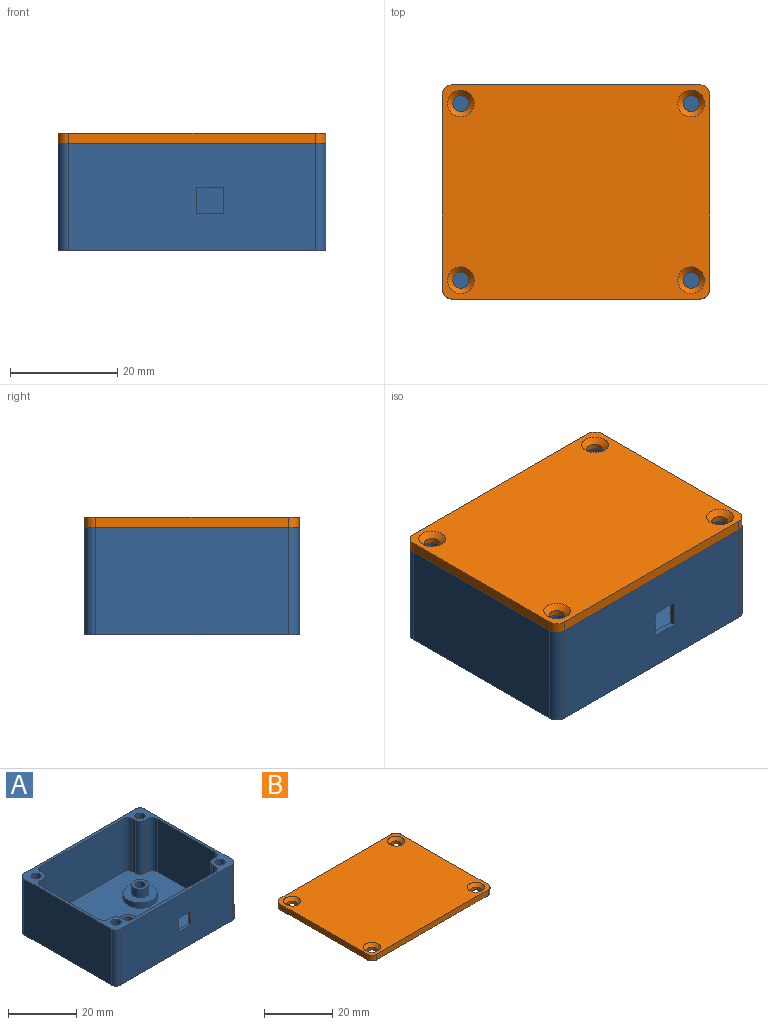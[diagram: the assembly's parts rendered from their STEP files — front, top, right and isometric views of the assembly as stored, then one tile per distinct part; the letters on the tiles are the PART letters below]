
ASSEMBLY  parts=2 mates=1
PART A: 71 faces, bbox 50x40x20 mm
  f0: plane 34x19mm, normal (0,1,0), area 621mm2, adj f4,f8,f56,f58,f67,f68,f69,f70
  f1: plane 46x20mm, normal (0,-1,0), area 895mm2, adj f8,f12,f52,f53,f67,f68,f69,f70
  f2: cylinder r=1.5mm len=4mm, axis (0,0,-1), area 37.7mm2, adj f30,f50
  f3: cylinder r=1.5mm len=4mm, axis (0,0,-1), area 37.7mm2, adj f32,f43
  f4: plane 48x38mm, normal (0,0,1), area 1563.5mm2, adj f0,f5,f6,f7,f13,f14,f15,f16
  f5: plane 24x19mm, normal (-1,0,0), area 456mm2, adj f4,f8,f60,f61
  f6: plane 34x19mm, normal (0,-1,0), area 646mm2, adj f4,f8,f62,f64
  f7: plane 24x19mm, normal (1,0,0), area 456mm2, adj f4,f8,f57,f66
  f8: plane 50x40mm, normal (0,0,1), area 247.7mm2, adj f0,f1,f5,f6,f7,f9,f10,f11
  f9: plane 46x20mm, normal (0,1,0), area 920mm2, adj f8,f12,f51,f54
  f10: plane 36x20mm, normal (-1,0,0), area 720mm2, adj f8,f12,f51,f52
  f11: plane 36x20mm, normal (1,0,0), area 720mm2, adj f8,f12,f53,f54
  f12: plane 50x40mm, normal (0,0,-1), area 1949.8mm2, adj f1,f9,f10,f11,f37,f38,f39,f40
  f13: plane 19x1mm, normal (0,-1,0), area 19mm2, adj f4,f8,f65,f66
  f14: plane 19x1mm, normal (1,0,0), area 19mm2, adj f4,f8,f64,f65
  f15: plane 19x1mm, normal (0,-1,0), area 19mm2, adj f4,f8,f61,f63
  f16: plane 19x1mm, normal (-1,0,0), area 19mm2, adj f4,f8,f62,f63
  f17: plane 19x1mm, normal (0,1,0), area 19mm2, adj f4,f8,f59,f60
  f18: plane 19x1mm, normal (-1,0,0), area 19mm2, adj f4,f8,f58,f59
  f19: plane 19x1mm, normal (0,1,0), area 19mm2, adj f4,f8,f55,f57
  f20: plane 19x1mm, normal (1,0,0), area 19mm2, adj f4,f8,f55,f56
  f21: cylinder r=1.5mm len=10mm, axis (0,0,1), area 94.2mm2, adj f8,f22
  f22: plane 3x3mm, normal (0,0,1), area 7.1mm2, adj f21
  f23: cylinder r=1.5mm len=10mm, axis (0,0,1), area 94.2mm2, adj f8,f24
  f24: plane 3x3mm, normal (0,0,1), area 7.1mm2, adj f23
  f25: cylinder r=1.5mm len=10mm, axis (0,0,1), area 94.2mm2, adj f8,f26
  f26: plane 3x3mm, normal (0,0,1), area 7.1mm2, adj f25
  f27: cylinder r=1.5mm len=10mm, axis (0,0,1), area 94.2mm2, adj f8,f28
  f28: plane 3x3mm, normal (0,0,1), area 7.1mm2, adj f27
  f29: cylinder r=2.5mm len=5mm, axis (0,0,-1), area 47.1mm2, adj f30,f34
  f30: plane 5x5mm, normal (0,0,1), area 12.6mm2, adj f2,f29
  f31: cylinder r=2.5mm len=5mm, axis (0,0,-1), area 47.1mm2, adj f32,f36
  f32: plane 5x5mm, normal (0,0,1), area 12.6mm2, adj f3,f31
  f33: cylinder r=5mm len=10mm, axis (0,0,-1), area 62.8mm2, adj f4,f34
  f34: plane 10x10mm, normal (0,0,1), area 58.9mm2, adj f29,f33
  f35: cylinder r=5mm len=10mm, axis (0,0,-1), area 62.8mm2, adj f4,f36
  f36: plane 10x10mm, normal (0,0,1), area 58.9mm2, adj f31,f35
  f37: plane 3x2mm, normal (0,-1,0), area 6mm2, adj f12,f38,f42,f43
  f38: plane 2.6x2mm, normal (-0.87,-0.5,0), area 6mm2, adj f12,f37,f39,f43
  f39: plane 2.6x2mm, normal (-0.87,0.5,0), area 6mm2, adj f12,f38,f40,f43
  f40: plane 3x2mm, normal (0,1,0), area 6mm2, adj f12,f39,f41,f43
  f41: plane 2.6x2mm, normal (0.87,0.5,0), area 6mm2, adj f12,f40,f42,f43
  f42: plane 2.6x2mm, normal (0.87,-0.5,0), area 6mm2, adj f12,f37,f41,f43
  f43: plane 6x5.2mm, normal (0,0,-1), area 16.3mm2, adj f3,f37,f38,f39,f40,f41,f42
  f44: plane 2.92x2mm, normal (0.24,-0.97,0), area 6mm2, adj f12,f45,f49,f50
  f45: plane 2.17x2.07mm, normal (-0.72,-0.69,0), area 6mm2, adj f12,f44,f46,f50
  f46: plane 2.88x2mm, normal (-0.96,0.28,0), area 6mm2, adj f12,f45,f47,f50
  f47: plane 2.92x2mm, normal (-0.24,0.97,0), area 6mm2, adj f12,f46,f48,f50
  f48: plane 2.17x2.07mm, normal (0.72,0.69,0), area 6mm2, adj f12,f47,f49,f50
  f49: plane 2.88x2mm, normal (0.96,-0.28,0), area 6mm2, adj f12,f44,f48,f50
  f50: plane 5.83x5.76mm, normal (0,0,-1), area 16.3mm2, adj f2,f44,f45,f46,f47,f48,f49
  f51: cylinder r=2mm len=20mm, axis (0,0,1), area 62.8mm2, adj f8,f9,f10,f12
  f52: cylinder r=2mm len=20mm, axis (0,0,-1), area 62.8mm2, adj f1,f8,f10,f12
  f53: cylinder r=2mm len=20mm, axis (0,0,1), area 62.8mm2, adj f1,f8,f11,f12
  f54: cylinder r=2mm len=20mm, axis (0,0,-1), area 62.8mm2, adj f8,f9,f11,f12
  f55: cylinder r=2mm len=19mm, axis (0,0,1), area 59.7mm2, adj f4,f8,f19,f20
  f56: cylinder r=2mm len=19mm, axis (0,0,-1), area 59.7mm2, adj f0,f4,f8,f20
  f57: cylinder r=2mm len=19mm, axis (0,0,-1), area 59.7mm2, adj f4,f7,f8,f19
  f58: cylinder r=2mm len=19mm, axis (0,0,1), area 59.7mm2, adj f0,f4,f8,f18
  f59: cylinder r=2mm len=19mm, axis (0,0,1), area 59.7mm2, adj f4,f8,f17,f18
  f60: cylinder r=2mm len=19mm, axis (0,0,-1), area 59.7mm2, adj f4,f5,f8,f17
  f61: cylinder r=2mm len=19mm, axis (0,0,1), area 59.7mm2, adj f4,f5,f8,f15
  f62: cylinder r=2mm len=19mm, axis (0,0,1), area 59.7mm2, adj f4,f6,f8,f16
  f63: cylinder r=2mm len=19mm, axis (0,0,1), area 59.7mm2, adj f4,f8,f15,f16
  f64: cylinder r=2mm len=19mm, axis (0,0,-1), area 59.7mm2, adj f4,f6,f8,f14
  f65: cylinder r=2mm len=19mm, axis (0,0,1), area 59.7mm2, adj f4,f8,f13,f14
  f66: cylinder r=2mm len=19mm, axis (0,0,1), area 59.7mm2, adj f4,f7,f8,f13
  f67: plane 5x1mm, normal (0,0,-1), area 5mm2, adj f0,f1,f68,f70
  f68: plane 5x1mm, normal (1,0,0), area 5mm2, adj f0,f1,f67,f69
  f69: plane 5x1mm, normal (0,0,1), area 5mm2, adj f0,f1,f68,f70
  f70: plane 5x1mm, normal (-1,0,0), area 5mm2, adj f0,f1,f67,f69
PART B: 18 faces, bbox 50x40x2 mm
  f0: plane 36x2mm, normal (-1,0,0), area 72mm2, adj f4,f5,f14,f17
  f1: plane 46x2mm, normal (0,-1,0), area 92mm2, adj f4,f5,f14,f15
  f2: plane 36x2mm, normal (1,0,0), area 72mm2, adj f4,f5,f15,f16
  f3: plane 46x2mm, normal (0,1,0), area 92mm2, adj f4,f5,f16,f17
  f4: plane 50x40mm, normal (0,0,1), area 1918mm2, adj f0,f1,f2,f3,f10,f11,f12,f13
  f5: plane 50x40mm, normal (0,0,-1), area 1968.3mm2, adj f0,f1,f2,f3,f6,f7,f8,f9
  f6: cylinder r=1.5mm len=3mm, axis (0,0,1), area 9.4mm2, adj f5,f13
  f7: cylinder r=1.5mm len=3mm, axis (0,0,1), area 9.4mm2, adj f5,f12
  f8: cylinder r=1.5mm len=3mm, axis (0,0,1), area 9.4mm2, adj f5,f11
  f9: cylinder r=1.5mm len=3mm, axis (0,0,1), area 9.4mm2, adj f5,f10
  f10: cone r=1.5mm half-angle=45deg, axis (0,0,1), area 17.8mm2, adj f4,f9
  f11: cone r=1.5mm half-angle=45deg, axis (0,0,1), area 17.8mm2, adj f4,f8
  f12: cone r=1.5mm half-angle=45deg, axis (0,0,1), area 17.8mm2, adj f4,f7
  f13: cone r=1.5mm half-angle=45deg, axis (0,0,1), area 17.8mm2, adj f4,f6
  f14: cylinder r=2mm len=2mm, axis (0,0,1), area 6.3mm2, adj f0,f1,f4,f5
  f15: cylinder r=2mm len=2mm, axis (0,0,-1), area 6.3mm2, adj f1,f2,f4,f5
  f16: cylinder r=2mm len=2mm, axis (0,0,1), area 6.3mm2, adj f2,f3,f4,f5
  f17: cylinder r=2mm len=2mm, axis (0,0,-1), area 6.3mm2, adj f0,f3,f4,f5
PLACE A at identity fixed
PLACE B t=(-76.05,-0.64,20)mm
MATE slider A.f25 <-> B.f8  axis (0,0,1) through (-18.81,22.08,20)mm
